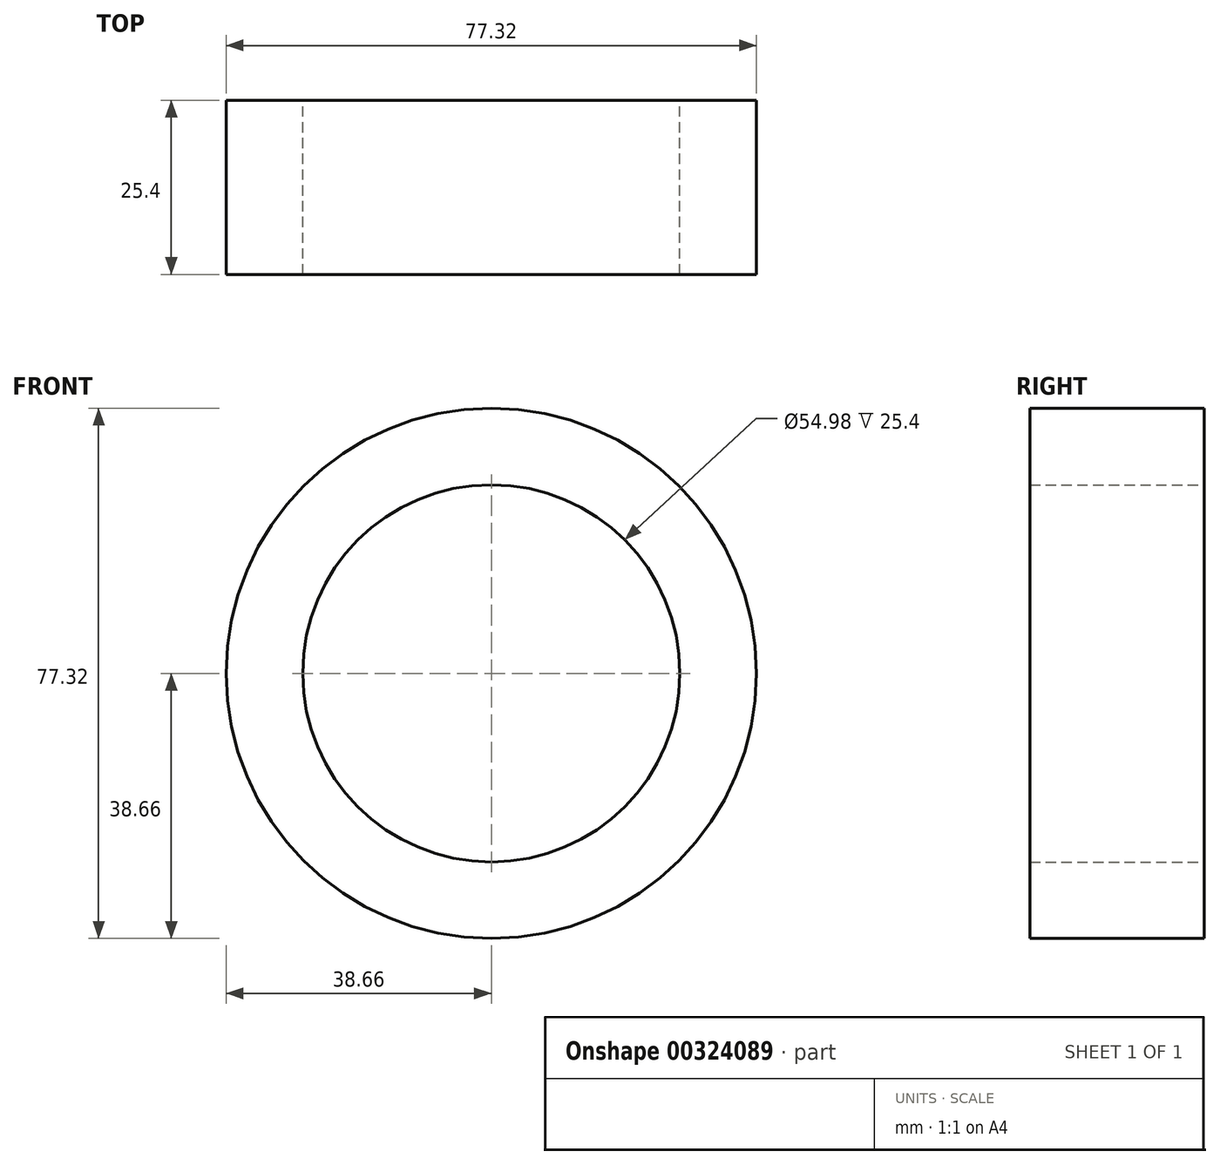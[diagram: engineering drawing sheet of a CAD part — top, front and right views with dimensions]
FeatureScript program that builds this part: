
annotation { "Feature Type Name" : "Feature", "Feature Type Description" : "" }
export const myFeature = defineFeature(function(context is Context, id is Id, definition is map)
    precondition{}
    {
        {
            var Q0;
            Q0=qCreatedBy(makeId("Front.planeOp"),FACE);
            var sketch = newSketch(context, id + "F0", { "sketchPlane" : qUnion([Q0])});
            skCircle(sketch, "E0", {"center": v(0, 0) * mm, "radius": 27.5 * mm});
            skCircle(sketch, "E1", {"center": v(0, 0) * mm, "radius": 38.66 * mm});
            skSolve(sketch);
        }
        {
            var Q0;
            Q0=makeQuery(id+"F0.imprint","IMPRINT",FACE,{"disambiguationData":[TD([[makeQuery(id+"F0.imprint","IMPRINT",EDGE,{"derivedFrom":sQuery(id+"F0.wireOp",EDGE,"E0")}),-1.0]])]});
            extrude(context, id + "F1", {"entities" : qUnion([Q0]), "depth" : 25.4 * mm});
        }
    });
